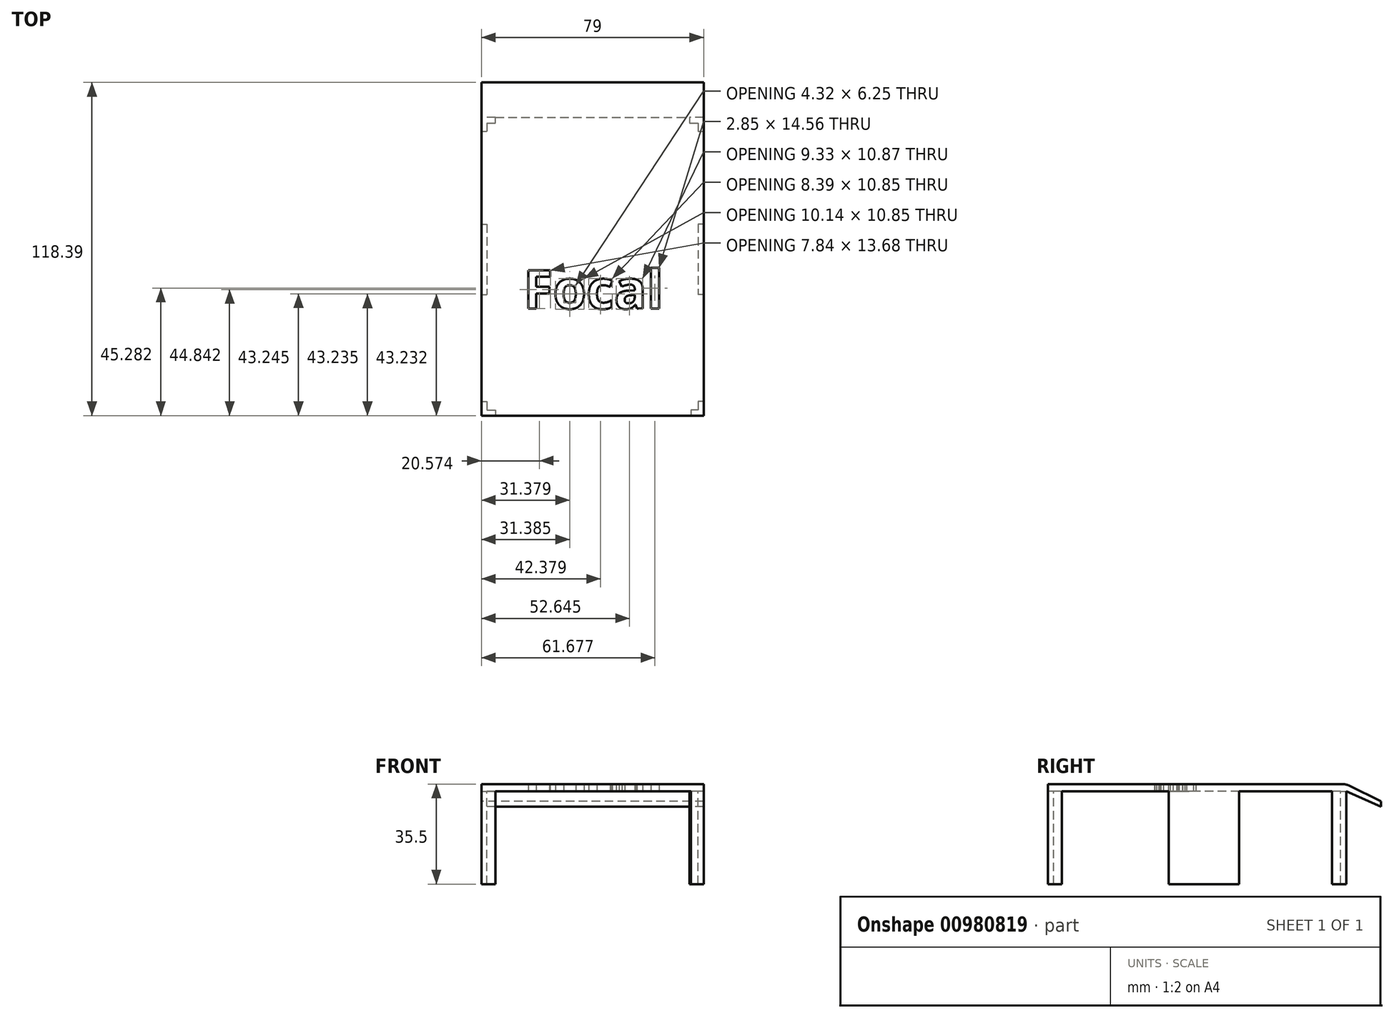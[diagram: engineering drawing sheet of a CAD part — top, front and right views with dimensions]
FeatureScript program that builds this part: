
annotation { "Feature Type Name" : "Feature", "Feature Type Description" : "" }
export const myFeature = defineFeature(function(context is Context, id is Id, definition is map)
    precondition{}
    {
        {
            var Q0;
            Q0=qCreatedBy(makeId("Top.planeOp"),FACE);
            var sketch = newSketch(context, id + "F0", { "sketchPlane" : qUnion([Q0])});
            skLineSegment(sketch, "E0.bottom", {"start": v(-39.5, 33.3) * mm, "end": v(39.5, 33.3) * mm});
            skLineSegment(sketch, "E0.top", {"start": v(-39.5, -72.7) * mm, "end": v(39.5, -72.7) * mm});
            skLineSegment(sketch, "E0.left", {"start": v(-39.5, 33.3) * mm, "end": v(-39.5, -72.7) * mm});
            skLineSegment(sketch, "E0.right", {"start": v(39.5, 33.3) * mm, "end": v(39.5, -72.7) * mm});
            skLineSegment(sketch, "E1.bottom", {"start": v(-39.5, 45.63) * mm, "end": v(39.5, 45.63) * mm});
            skLineSegment(sketch, "E1.left", {"start": v(-39.5, 45.63) * mm, "end": v(-39.5, 33.3) * mm});
            skLineSegment(sketch, "E1.right", {"start": v(39.5, 45.63) * mm, "end": v(39.5, 33.3) * mm});
            skLineSegment(sketch, "E2.bottom", {"start": v(-39.5, 33.3) * mm, "end": v(-37.5, 33.3) * mm});
            skLineSegment(sketch, "E2.top", {"start": v(-39.5, 28.3) * mm, "end": v(-37.5, 28.3) * mm});
            skLineSegment(sketch, "E2.left", {"start": v(-39.5, 33.3) * mm, "end": v(-39.5, 28.3) * mm});
            skLineSegment(sketch, "E2.right", {"start": v(-37.5, 33.3) * mm, "end": v(-37.5, 28.3) * mm});
            skLineSegment(sketch, "E3.bottom", {"start": v(37.5, 33.3) * mm, "end": v(39.5, 33.3) * mm});
            skLineSegment(sketch, "E3.top", {"start": v(37.5, 28.3) * mm, "end": v(39.5, 28.3) * mm});
            skLineSegment(sketch, "E3.left", {"start": v(37.5, 33.3) * mm, "end": v(37.5, 28.3) * mm});
            skLineSegment(sketch, "E3.right", {"start": v(39.5, 33.3) * mm, "end": v(39.5, 28.3) * mm});
            skLineSegment(sketch, "E4.bottom", {"start": v(-39.5, -67.7) * mm, "end": v(-37.5, -67.7) * mm});
            skLineSegment(sketch, "E4.top", {"start": v(-39.5, -72.7) * mm, "end": v(-37.5, -72.7) * mm});
            skLineSegment(sketch, "E4.left", {"start": v(-39.5, -67.7) * mm, "end": v(-39.5, -72.7) * mm});
            skLineSegment(sketch, "E4.right", {"start": v(-37.5, -67.7) * mm, "end": v(-37.5, -72.7) * mm});
            skLineSegment(sketch, "E5.bottom", {"start": v(39.5, -67.7) * mm, "end": v(37.5, -67.7) * mm});
            skLineSegment(sketch, "E5.top", {"start": v(39.5, -72.7) * mm, "end": v(37.5, -72.7) * mm});
            skLineSegment(sketch, "E5.left", {"start": v(39.5, -67.7) * mm, "end": v(39.5, -72.7) * mm});
            skLineSegment(sketch, "E5.right", {"start": v(37.5, -67.7) * mm, "end": v(37.5, -72.7) * mm});
            skLineSegment(sketch, "E6.bottom", {"start": v(-39.5, -4.7) * mm, "end": v(-37.5, -4.7) * mm});
            skLineSegment(sketch, "E6.top", {"start": v(-39.5, -29.7) * mm, "end": v(-37.5, -29.7) * mm});
            skLineSegment(sketch, "E6.left", {"start": v(-39.5, -4.7) * mm, "end": v(-39.5, -29.7) * mm});
            skLineSegment(sketch, "E6.right", {"start": v(-37.5, -4.7) * mm, "end": v(-37.5, -29.7) * mm});
            skLineSegment(sketch, "E7.bottom", {"start": v(39.5, -4.7) * mm, "end": v(37.5, -4.7) * mm});
            skLineSegment(sketch, "E7.top", {"start": v(39.5, -29.7) * mm, "end": v(37.5, -29.7) * mm});
            skLineSegment(sketch, "E7.left", {"start": v(39.5, -4.7) * mm, "end": v(39.5, -29.7) * mm});
            skLineSegment(sketch, "E7.right", {"start": v(37.5, -4.7) * mm, "end": v(37.5, -29.7) * mm});
            skText(sketch, "E8", { "text": "Focal", "fontName": "OpenSans-Bold.ttf"});
            skLineSegment(sketch, "E9", {"start": v(-37.5, 28.3) * mm, "end": v(-37.5, -67.7) * mm});
            skLineSegment(sketch, "E10", {"start": v(37.5, 28.3) * mm, "end": v(37.5, -67.7) * mm});
            skLineSegment(sketch, "E11.bottom", {"start": v(-37.5, 31.3) * mm, "end": v(-34.5, 31.3) * mm});
            skLineSegment(sketch, "E11.top", {"start": v(-37.5, 33.3) * mm, "end": v(-34.5, 33.3) * mm});
            skLineSegment(sketch, "E11.left", {"start": v(-37.5, 31.3) * mm, "end": v(-37.5, 33.3) * mm});
            skLineSegment(sketch, "E11.right", {"start": v(-34.5, 31.3) * mm, "end": v(-34.5, 33.3) * mm});
            skLineSegment(sketch, "E12.bottom", {"start": v(34.5, 33.3) * mm, "end": v(37.5, 33.3) * mm});
            skLineSegment(sketch, "E12.top", {"start": v(34.5, 31.3) * mm, "end": v(37.5, 31.3) * mm});
            skLineSegment(sketch, "E12.left", {"start": v(34.5, 33.3) * mm, "end": v(34.5, 31.3) * mm});
            skLineSegment(sketch, "E12.right", {"start": v(37.5, 33.3) * mm, "end": v(37.5, 31.3) * mm});
            skLineSegment(sketch, "E13.bottom", {"start": v(37.5, -70.7) * mm, "end": v(35, -70.7) * mm});
            skLineSegment(sketch, "E13.top", {"start": v(37.5, -72.7) * mm, "end": v(35, -72.7) * mm});
            skLineSegment(sketch, "E13.left", {"start": v(37.5, -70.7) * mm, "end": v(37.5, -72.7) * mm});
            skLineSegment(sketch, "E13.right", {"start": v(35, -70.7) * mm, "end": v(35, -72.7) * mm});
            skLineSegment(sketch, "E14.top", {"start": v(-37.5, -72.7) * mm, "end": v(-32.16, -72.7) * mm});
            skLineSegment(sketch, "E14.left", {"start": v(-37.5, -70.2) * mm, "end": v(-37.5, -72.7) * mm});
            skLineSegment(sketch, "E15.bottom", {"start": v(-37.5, -70.7) * mm, "end": v(-34.5, -70.7) * mm});
            skLineSegment(sketch, "E15.top", {"start": v(-37.5, -72.7) * mm, "end": v(-34.5, -72.7) * mm});
            skLineSegment(sketch, "E15.left", {"start": v(-37.5, -70.7) * mm, "end": v(-37.5, -72.7) * mm});
            skLineSegment(sketch, "E15.right", {"start": v(-34.5, -70.7) * mm, "end": v(-34.5, -72.7) * mm});
            skLineSegment(sketch, "E16", {"start": v(-34.5, -70.7) * mm, "end": v(35, -70.7) * mm});
            skLineSegment(sketch, "E17", {"start": v(-34.5, 31.3) * mm, "end": v(34.5, 31.3) * mm});
            const initialGuessF0  = {"E8": [-0.02457, -0.0347, 1, 0, 0.0138]};
            skSetInitialGuess(sketch, initialGuessF0);
            skSolve(sketch);
        }
        {
            var Q0;
            {var subQ1=sQuery(id+"F0.wireOp",EDGE,"E2.top");Q0=makeQuery(id+"F0.imprint","IMPRINT",FACE,{"disambiguationData":[TD([[makeQuery(id+"F0.imprint","IMPRINT",EDGE,{"derivedFrom":subQ1}),1.0]])]});}
            var Q1;
            {var subQ0=sQuery(id+"F0.wireOp",EDGE,"E2.top");Q1=makeQuery(id+"F0.imprint","IMPRINT",FACE,{"disambiguationData":[TD([[makeQuery(id+"F0.imprint","IMPRINT",EDGE,{"derivedFrom":subQ0}),-1.0]])]});}
            var Q2;
            {var subQ2=sQuery(id+"F0.wireOp",EDGE,"E6.bottom");Q2=makeQuery(id+"F0.imprint","IMPRINT",FACE,{"disambiguationData":[TD([[makeQuery(id+"F0.imprint","IMPRINT",EDGE,{"derivedFrom":subQ2}),-1.0]])]});}
            var Q3;
            {var subQ2=sQuery(id+"F0.wireOp",EDGE,"E4.bottom");Q3=makeQuery(id+"F0.imprint","IMPRINT",FACE,{"disambiguationData":[TD([[makeQuery(id+"F0.imprint","IMPRINT",EDGE,{"derivedFrom":subQ2}),1.0]])]});}
            var Q4;
            {var subQ1=sQuery(id+"F0.wireOp",EDGE,"E4.bottom");Q4=makeQuery(id+"F0.imprint","IMPRINT",FACE,{"disambiguationData":[TD([[makeQuery(id+"F0.imprint","IMPRINT",EDGE,{"derivedFrom":subQ1}),-1.0]])]});}
            var Q5;
            {var subQ0=sQuery(id+"F0.wireOp",EDGE,"E13.right");Q5=makeQuery(id+"F0.imprint","IMPRINT",FACE,{"disambiguationData":[TD([[makeQuery(id+"F0.imprint","IMPRINT",EDGE,{"derivedFrom":subQ0}),-1.0]])]});}
            var Q6;
            {var subQ1=sQuery(id+"F0.wireOp",EDGE,"E5.bottom");Q6=makeQuery(id+"F0.imprint","IMPRINT",FACE,{"disambiguationData":[TD([[makeQuery(id+"F0.imprint","IMPRINT",EDGE,{"derivedFrom":subQ1}),1.0]])]});}
            var Q7;
            {var subQ2=sQuery(id+"F0.wireOp",EDGE,"E5.bottom");Q7=makeQuery(id+"F0.imprint","IMPRINT",FACE,{"disambiguationData":[TD([[makeQuery(id+"F0.imprint","IMPRINT",EDGE,{"derivedFrom":subQ2}),-1.0]])]});}
            var Q8;
            {var subQ2=sQuery(id+"F0.wireOp",EDGE,"E7.bottom");Q8=makeQuery(id+"F0.imprint","IMPRINT",FACE,{"disambiguationData":[TD([[makeQuery(id+"F0.imprint","IMPRINT",EDGE,{"derivedFrom":subQ2}),1.0]])]});}
            var Q9;
            {var subQ0=sQuery(id+"F0.wireOp",EDGE,"E3.top");Q9=makeQuery(id+"F0.imprint","IMPRINT",FACE,{"disambiguationData":[TD([[makeQuery(id+"F0.imprint","IMPRINT",EDGE,{"derivedFrom":subQ0}),-1.0]])]});}
            var Q10;
            {var subQ0=sQuery(id+"F0.wireOp",EDGE,"E3.top");Q10=makeQuery(id+"F0.imprint","IMPRINT",FACE,{"disambiguationData":[TD([[makeQuery(id+"F0.imprint","IMPRINT",EDGE,{"derivedFrom":subQ0}),1.0]])]});}
            var Q11;
            {var subQ4=sQuery(id+"F0.wireOp",EDGE,"E11.bottom");Q11=makeQuery(id+"F0.imprint","IMPRINT",FACE,{"disambiguationData":[TD([[makeQuery(id+"F0.imprint","IMPRINT",EDGE,{"derivedFrom":subQ4}),1.0]])]});}
            var Q12;
            {var subQ4=sQuery(id+"F0.wireOp",EDGE,"E15.bottom");Q12=makeQuery(id+"F0.imprint","IMPRINT",FACE,{"disambiguationData":[TD([[makeQuery(id+"F0.imprint","IMPRINT",EDGE,{"derivedFrom":subQ4}),-1.0]])]});}
            var Q13;
            {var subQ4=sQuery(id+"F0.wireOp",EDGE,"E13.bottom");Q13=makeQuery(id+"F0.imprint","IMPRINT",FACE,{"disambiguationData":[TD([[makeQuery(id+"F0.imprint","IMPRINT",EDGE,{"derivedFrom":subQ4}),1.0]])]});}
            var Q14;
            {var subQ4=sQuery(id+"F0.wireOp",EDGE,"E12.top");Q14=makeQuery(id+"F0.imprint","IMPRINT",FACE,{"disambiguationData":[TD([[makeQuery(id+"F0.imprint","IMPRINT",EDGE,{"derivedFrom":subQ4}),1.0]])]});}
            var Q15;
            Q15=makeQuery(id+"F0.imprint","IMPRINT",FACE,{"disambiguationData":[TD([[makeQuery(id+"F0.imprint","IMPRINT",EDGE,{"derivedFrom":sQuery(id+"F0.wireOp",EDGE,"E8.sketch_text.stroke-10")}),1.0]])]});
            var Q16;
            Q16=makeQuery(id+"F0.imprint","IMPRINT",FACE,{"disambiguationData":[TD([[makeQuery(id+"F0.imprint","IMPRINT",EDGE,{"derivedFrom":sQuery(id+"F0.wireOp",EDGE,"E8.sketch_text.stroke-60")}),1.0]])]});
            var Q17;
            {var subQ8=sQuery(id+"F0.wireOp",EDGE,"E6.right");Q17=makeQuery(id+"F0.imprint","IMPRINT",FACE,{"disambiguationData":[TD([[makeQuery(id+"F0.imprint","IMPRINT",EDGE,{"derivedFrom":subQ8}),1.0]])]});}
            var Q18;
            {var subQ0=sQuery(id+"F0.wireOp",EDGE,"E11.right");Q18=makeQuery(id+"F0.imprint","IMPRINT",FACE,{"disambiguationData":[TD([[makeQuery(id+"F0.imprint","IMPRINT",EDGE,{"derivedFrom":subQ0}),-1.0]])]});}
            extrude(context, id + "F1", {"entities" : qUnion([Q0, Q1, Q2, Q3, Q4, Q5, Q6, Q7, Q8, Q9, Q10, Q11, Q12, Q13, Q14, Q15, Q16, Q17, Q18]), "depth" : 2.5 * mm, "offsetDistance" : 25 * mm});
        }
        {
            var Q0;
            Q0=qCreatedBy(makeId("Right.planeOp"),FACE);
            var sketch = newSketch(context, id + "F2", { "sketchPlane" : qUnion([Q0])});
            skLineSegment(sketch, "E18", {"start": v(33.3, 2.5) * mm, "end": v(45.69, -3.55) * mm});
            skLineSegment(sketch, "E19", {"start": v(45.69, -3.55) * mm, "end": v(45.69, -5.45) * mm});
            skLineSegment(sketch, "E20", {"start": v(45.69, -5.45) * mm, "end": v(33.3, 0) * mm});
            skLineSegment(sketch, "E21", {"start": v(33.3, 2.5) * mm, "end": v(33.3, 0) * mm});
            skSolve(sketch);
        }
        {
            var Q0;
            Q0=makeQuery(id+"F2.imprint","IMPRINT",FACE,{"disambiguationData":[TD([[makeQuery(id+"F2.imprint","IMPRINT",EDGE,{"derivedFrom":sQuery(id+"F2.wireOp",EDGE,"E18")}),-1.0]])]});
            extrude(context, id + "F3", {"entities" : qUnion([Q0]), "operationType" : NewBodyOperationType.ADD, "endBound" : BoundingType.SYMMETRIC, "depth" : 79 * mm, "offsetDistance" : 25 * mm});
        }
        {
            var Q0;
            {var subQ4=sQuery(id+"F0.wireOp",EDGE,"E12.top");Q0=makeQuery(id+"F0.imprint","IMPRINT",FACE,{"disambiguationData":[TD([[makeQuery(id+"F0.imprint","IMPRINT",EDGE,{"derivedFrom":subQ4}),1.0]])]});}
            var Q1;
            {var subQ0=sQuery(id+"F0.wireOp",EDGE,"E3.top");Q1=makeQuery(id+"F0.imprint","IMPRINT",FACE,{"disambiguationData":[TD([[makeQuery(id+"F0.imprint","IMPRINT",EDGE,{"derivedFrom":subQ0}),1.0]])]});}
            var Q2;
            {var subQ1=sQuery(id+"F0.wireOp",EDGE,"E2.top");Q2=makeQuery(id+"F0.imprint","IMPRINT",FACE,{"disambiguationData":[TD([[makeQuery(id+"F0.imprint","IMPRINT",EDGE,{"derivedFrom":subQ1}),1.0]])]});}
            var Q3;
            {var subQ4=sQuery(id+"F0.wireOp",EDGE,"E11.bottom");Q3=makeQuery(id+"F0.imprint","IMPRINT",FACE,{"disambiguationData":[TD([[makeQuery(id+"F0.imprint","IMPRINT",EDGE,{"derivedFrom":subQ4}),1.0]])]});}
            var Q4;
            {var subQ2=sQuery(id+"F0.wireOp",EDGE,"E6.bottom");Q4=makeQuery(id+"F0.imprint","IMPRINT",FACE,{"disambiguationData":[TD([[makeQuery(id+"F0.imprint","IMPRINT",EDGE,{"derivedFrom":subQ2}),-1.0]])]});}
            var Q5;
            {var subQ2=sQuery(id+"F0.wireOp",EDGE,"E7.bottom");Q5=makeQuery(id+"F0.imprint","IMPRINT",FACE,{"disambiguationData":[TD([[makeQuery(id+"F0.imprint","IMPRINT",EDGE,{"derivedFrom":subQ2}),1.0]])]});}
            var Q6;
            {var subQ1=sQuery(id+"F0.wireOp",EDGE,"E5.bottom");Q6=makeQuery(id+"F0.imprint","IMPRINT",FACE,{"disambiguationData":[TD([[makeQuery(id+"F0.imprint","IMPRINT",EDGE,{"derivedFrom":subQ1}),1.0]])]});}
            var Q7;
            {var subQ4=sQuery(id+"F0.wireOp",EDGE,"E13.bottom");Q7=makeQuery(id+"F0.imprint","IMPRINT",FACE,{"disambiguationData":[TD([[makeQuery(id+"F0.imprint","IMPRINT",EDGE,{"derivedFrom":subQ4}),1.0]])]});}
            var Q8;
            {var subQ4=sQuery(id+"F0.wireOp",EDGE,"E15.bottom");Q8=makeQuery(id+"F0.imprint","IMPRINT",FACE,{"disambiguationData":[TD([[makeQuery(id+"F0.imprint","IMPRINT",EDGE,{"derivedFrom":subQ4}),-1.0]])]});}
            var Q9;
            {var subQ1=sQuery(id+"F0.wireOp",EDGE,"E4.bottom");Q9=makeQuery(id+"F0.imprint","IMPRINT",FACE,{"disambiguationData":[TD([[makeQuery(id+"F0.imprint","IMPRINT",EDGE,{"derivedFrom":subQ1}),-1.0]])]});}
            extrude(context, id + "F4", {"entities" : qUnion([Q0, Q1, Q2, Q3, Q4, Q5, Q6, Q7, Q8, Q9]), "operationType" : NewBodyOperationType.ADD, "oppositeDirection" : true, "depth" : 33 * mm, "offsetDistance" : 25 * mm});
        }
        {
            var Q0;
            Q0=makeQuery(id+"F0.imprint","IMPRINT",FACE,{"disambiguationData":[TD([[makeQuery(id+"F0.imprint","IMPRINT",EDGE,{"derivedFrom":sQuery(id+"F0.wireOp",EDGE,"E8.sketch_text.stroke-0")}),-1.0]])]});
            var Q1;
            Q1=makeQuery(id+"F0.imprint","IMPRINT",FACE,{"disambiguationData":[TD([[makeQuery(id+"F0.imprint","IMPRINT",EDGE,{"derivedFrom":sQuery(id+"F0.wireOp",EDGE,"E8.sketch_text.stroke-10")}),-1.0]])]});
            var Q2;
            Q2=makeQuery(id+"F0.imprint","IMPRINT",FACE,{"disambiguationData":[TD([[makeQuery(id+"F0.imprint","IMPRINT",EDGE,{"derivedFrom":sQuery(id+"F0.wireOp",EDGE,"E8.sketch_text.stroke-28")}),-1.0]])]});
            var Q3;
            Q3=makeQuery(id+"F0.imprint","IMPRINT",FACE,{"disambiguationData":[TD([[makeQuery(id+"F0.imprint","IMPRINT",EDGE,{"derivedFrom":sQuery(id+"F0.wireOp",EDGE,"E8.sketch_text.stroke-42")}),-1.0]])]});
            var Q4;
            Q4=makeQuery(id+"F0.imprint","IMPRINT",FACE,{"disambiguationData":[TD([[makeQuery(id+"F0.imprint","IMPRINT",EDGE,{"derivedFrom":sQuery(id+"F0.wireOp",EDGE,"E8.sketch_text.stroke-67")}),-1.0]])]});
            extrude(context, id + "F5", {"entities" : qUnion([Q0, Q1, Q2, Q3, Q4]), "depth" : 2.35 * mm, "offsetDistance" : 25 * mm});
        }
        {
            var Q0;
            Q0=makeQuery(id+"F3.boolean.opBoolean","MERGE",EDGE,{"derivedFrom":[makeQuery(id+"F1.opExtrude","CAP_EDGE",EDGE,{"disambiguationData":[OSD([sQuery(id+"F0.wireOp",EDGE,"E0.bottom")])],"isStart":false}),makeQuery(id+"F3.opExtrude","SWEPT_EDGE",EDGE,{"disambiguationData":[OSD([sQuery(id+"F2.wireOp",EDGE,"E18"),sQuery(id+"F2.wireOp",EDGE,"E21")])]})]});
            fillet(context, id + "F6", {"entities" : qUnion([Q0]), "radius" : 5 * mm, "tangentPropagation" : true, "allowEdgeOverflow" : false});
        }
    });
